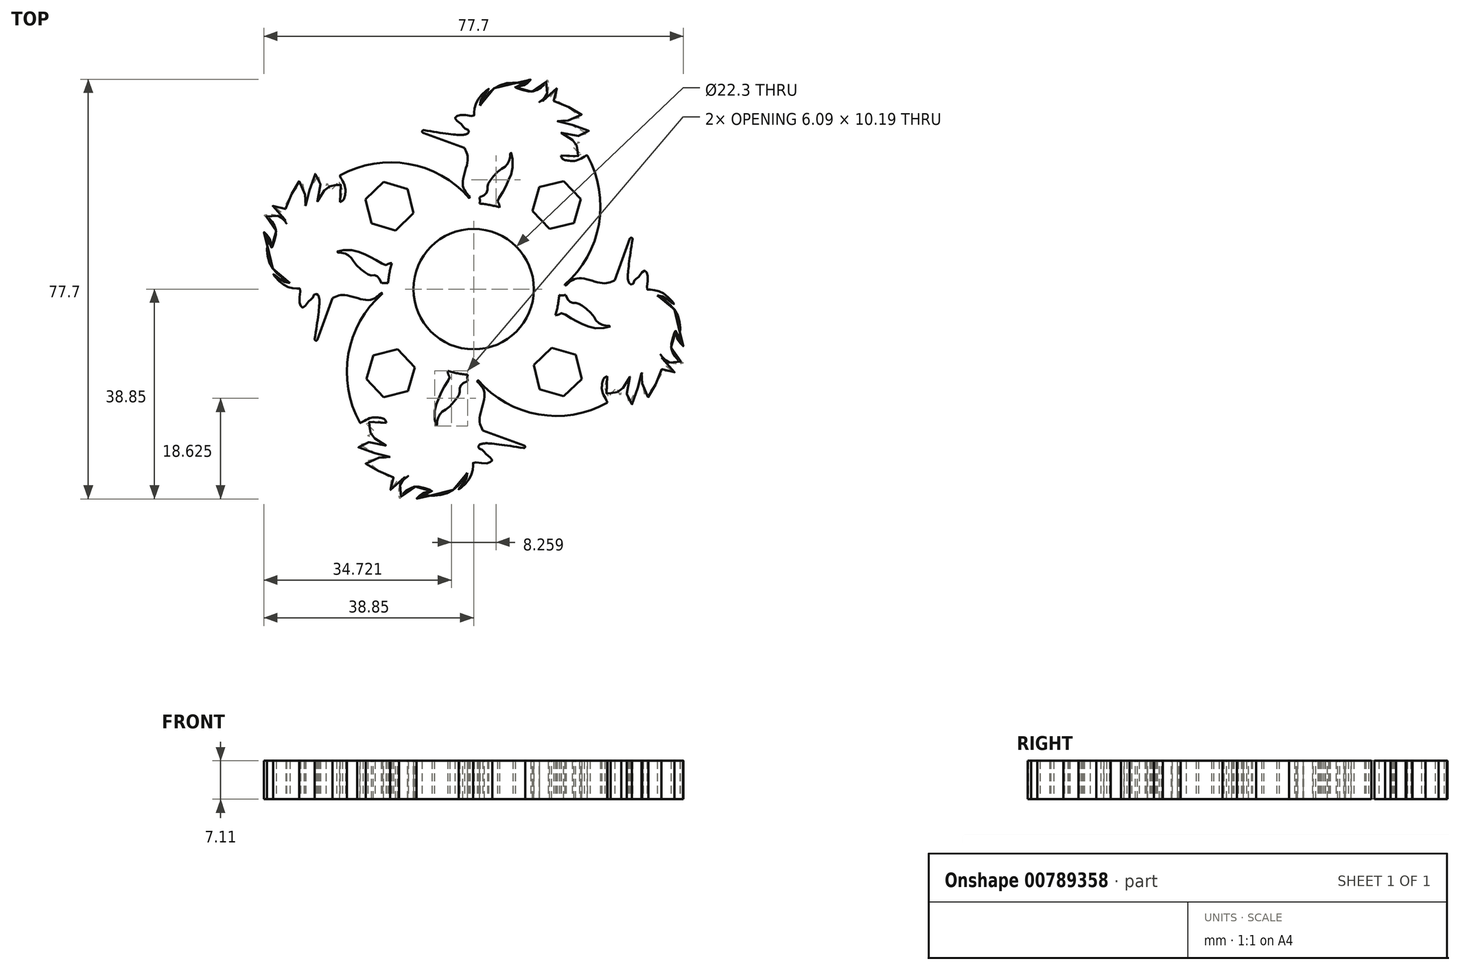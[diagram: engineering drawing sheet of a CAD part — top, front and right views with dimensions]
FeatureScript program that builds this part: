
annotation { "Feature Type Name" : "Feature", "Feature Type Description" : "" }
export const myFeature = defineFeature(function(context is Context, id is Id, definition is map)
    precondition{}
    {
        {
            var Q0;
            Q0=qCreatedBy(makeId("Top.planeOp"),FACE);
            var sketch = newSketch(context, id + "F0", { "sketchPlane" : qUnion([Q0])});
            skCircle(sketch, "E0", {"center": v(0, 0) * mm, "radius": 11.15 * mm});
            skLineSegment(sketch, "E1", {"start": v(-24.57, 4.35) * mm, "end": v(-20.17, 10.05) * mm});
            skFitSpline(sketch, "E2", {"points": [v(-20.17, 10.05) * mm, v(-18.6, 9.94) * mm, v(-15.83, 8.42) * mm, v(-13.83, 9.06) * mm], "startDerivative": vector(5.21, 0.73) * mm, "endDerivative": vector(5.8, 3.1) * mm});
            skFitSpline(sketch, "E3", {"points": [v(-21.73, 10.94) * mm, v(-21.9, 11.16) * mm, v(-22.2, 11.13) * mm, v(-22.5, 10.76) * mm, v(-22.9, 10.66) * mm, v(-23.94, 10.03) * mm, v(-24.16, 10.26) * mm, v(-24.15, 11) * mm, v(-23.6, 12.33) * mm, v(-23.83, 12.46) * mm, v(-24.69, 12.84) * mm, v(-25.7, 13.9) * mm, v(-26.21, 15.08) * mm, v(-25.72, 14.44) * mm, v(-24.6, 13.44) * mm], "startDerivative": vector(-3.17, 6.23) * mm, "endDerivative": vector(14.4, -3.3) * mm});
            skFitSpline(sketch, "E4", {"points": [v(-24.6, 13.44) * mm, v(-25.33, 14.36) * mm, v(-26.15, 16.1) * mm, v(-26.07, 18.07) * mm, v(-25.72, 19.07) * mm, v(-25.69, 19.78) * mm, v(-25.75, 20.4) * mm, v(-25.54, 20.07) * mm, v(-25.3, 19.05) * mm, v(-25.4, 18.27) * mm, v(-25.03, 18.7) * mm, v(-24.28, 19.98) * mm, v(-24.28, 20.88) * mm, v(-24.65, 21.87) * mm, v(-25.05, 22.32) * mm, v(-24.8, 22.35) * mm, v(-23.66, 21.93) * mm, v(-22.9, 21) * mm, v(-22.74, 20.53) * mm, v(-22.83, 21.43) * mm, v(-23.24, 22.55) * mm, v(-23.71, 23.15) * mm, v(-23.4, 23.08) * mm, v(-22.66, 22.69) * mm, v(-22.32, 22.3) * mm, v(-22.2, 22.57) * mm, v(-21.49, 23.56) * mm, v(-20.6, 23.98) * mm, v(-19.98, 24.29) * mm, v(-19.7, 25.05) * mm, v(-19.48, 24.85) * mm, v(-19.34, 24.17) * mm, v(-19.56, 23.08) * mm, v(-19.9, 22.45) * mm, v(-19.92, 21.83) * mm, v(-19.77, 22.07) * mm, v(-19.54, 22.84) * mm, v(-19.1, 23.35) * mm, v(-18.25, 23.98) * mm, v(-17.72, 24.53) * mm, v(-17.42, 25.42) * mm, v(-17.2, 25.15) * mm, v(-17.17, 24.49) * mm, v(-17.5, 23.32) * mm, v(-18.08, 22.55) * mm, v(-18.3, 21.99) * mm, v(-18.14, 22.2) * mm, v(-17.7, 22.6) * mm, v(-17.04, 23.03) * mm, v(-16.8, 23.18) * mm, v(-16.56, 23.76) * mm, v(-16.33, 23.57) * mm, v(-16.27, 22.94) * mm, v(-16.3, 22.75) * mm, v(-15.83, 22.91) * mm, v(-15.39, 23.3) * mm, v(-15.14, 23.95) * mm, v(-15.03, 23.57) * mm, v(-14.9, 22.84) * mm, v(-15.1, 21.82) * mm, v(-15.66, 21.08) * mm], "startDerivative": vector(-33.95, 39.33) * mm, "endDerivative": vector(-32.89, -35.92) * mm});
            skFitSpline(sketch, "E5", {"points": [v(-15.66, 21.08) * mm, v(-15.17, 21.19) * mm, v(-14.76, 21.8) * mm, v(-14.5, 22.9) * mm, v(-14.68, 24.18) * mm, v(-14.25, 23.59) * mm, v(-14, 22) * mm, v(-14.5, 20.36) * mm, v(-14.57, 19.83) * mm, v(-13.94, 18.55) * mm, v(-13.41, 17.15) * mm, v(-12.84, 15.14) * mm, v(-12.49, 12.77) * mm, v(-12.64, 11.92) * mm, v(-13.48, 12.77) * mm, v(-14.73, 14) * mm, v(-16.34, 15.07) * mm, v(-17.93, 15.31) * mm, v(-17.66, 15.14) * mm, v(-17.17, 14.94) * mm, v(-16.75, 14.58) * mm, v(-16.42, 14.04) * mm, v(-16.26, 13.35) * mm, v(-15.56, 12.1) * mm, v(-15.13, 11.54) * mm, v(-14.8, 11.28) * mm, v(-14.4, 11.16) * mm, v(-14.07, 10.94) * mm, v(-13.86, 10.42) * mm, v(-13.83, 9.06) * mm], "startDerivative": vector(21.3, 0.89) * mm, "endDerivative": vector(-1, -37.46) * mm});
            skFitSpline(sketch, "E6", {"points": [v(-21.73, 10.94) * mm, v(-21.72, 10.6) * mm, v(-21.92, 9.84) * mm, v(-24.57, 4.35) * mm], "startDerivative": vector(0.16, -2.17) * mm, "endDerivative": vector(-5.4, -10.67) * mm});
            skLineSegment(sketch, "E7.0", {"start": v(-15.45, 21.3) * mm, "end": v(-15.17, 21.19) * mm, "construction": true});
            skLineSegment(sketch, "E8.0", {"start": v(-22.2, 11.13) * mm, "end": v(-21.73, 10.94) * mm, "construction": true});
            skArc(sketch, "E9", {"start": v(0, 15.88) * mm, "mid": v(-5.79, 22.77) * mm, "end": v(-14.68, 24.18) * mm});
            skCircle(sketch, "E10", {"center": v(0, 0) * mm, "radius": 15.88 * mm});
            skArc(sketch, "E11", {"start": v(-11.09, 11.36) * mm, "mid": v(-11.77, 11.9) * mm, "end": v(-12.64, 11.92) * mm});
            skArc(sketch, "E12", {"start": v(-12.72, 9.5) * mm, "mid": v(-13.24, 9.8) * mm, "end": v(-13.82, 9.94) * mm});
            skArc(sketch, "E13", {"start": v(-13.54, 8.29) * mm, "mid": v(-13.89, 8.57) * mm, "end": v(-14.24, 8.84) * mm});
            skLineSegment(sketch, "E14", {"start": v(0, 15.88) * mm, "end": v(0, 11.15) * mm});
            skLineSegment(sketch, "E15", {"start": v(-15.88, 0) * mm, "end": v(-11.15, 0) * mm});
            skArc(sketch, "E16", {"start": v(0, 11.15) * mm, "mid": v(-7.88, 7.88) * mm, "end": v(-11.15, 0) * mm});
            skArc(sketch, "E17", {"start": v(0, 15.88) * mm, "mid": v(-11.23, 11.23) * mm, "end": v(-15.88, 0) * mm});
            skSolve(sketch);
        }
        {
            var Q0;
            {var subQ0=sQuery(id+"F0.wireOp",EDGE,"E9");var subQ1=sQuery(id+"F0.wireOp",EDGE,"E5");var subQ2=makeQuery(id+"F0.imprint","INTERSECT",VERTEX,{"disambiguationData":[OD(0.0)],"derivedFrom":[subQ1,subQ0]});Q0=makeQuery(id+"F0.imprint","IMPRINT",FACE,{"disambiguationData":[TD([[makeQuery(id+"F0.imprint","IMPRINT",EDGE,{"disambiguationData":[TD([[subQ2,-1.0]])],"derivedFrom":subQ1}),-1.0]])]});}
            var Q1;
            {var subQ0=sQuery(id+"F0.wireOp",EDGE,"E12");Q1=makeQuery(id+"F0.imprint","IMPRINT",FACE,{"disambiguationData":[TD([[makeQuery(id+"F0.imprint","IMPRINT",EDGE,{"derivedFrom":subQ0}),1.0]])]});}
            var Q2;
            {var subQ0=sQuery(id+"F0.wireOp",EDGE,"E9");var subQ1=sQuery(id+"F0.wireOp",EDGE,"E5");var subQ2=makeQuery(id+"F0.imprint","INTERSECT",VERTEX,{"disambiguationData":[OD(1.0)],"derivedFrom":[subQ1,subQ0]});Q2=makeQuery(id+"F0.imprint","IMPRINT",FACE,{"disambiguationData":[TD([[makeQuery(id+"F0.imprint","IMPRINT",EDGE,{"disambiguationData":[TD([[subQ2,-1.0]])],"derivedFrom":subQ1}),1.0]])]});}
            var Q3;
            {var subQ11=sQuery(id+"F0.wireOp",EDGE,"E1");Q3=makeQuery(id+"F0.imprint","IMPRINT",FACE,{"disambiguationData":[TD([[makeQuery(id+"F0.imprint","IMPRINT",EDGE,{"derivedFrom":subQ11}),1.0]])]});}
            extrude(context, id + "F1", {"entities" : qUnion([Q0, Q1, Q2, Q3]), "depth" : 10.16 * mm, "offsetDistance" : 25.4 * mm});
        }
        {
            var Q0;
            Q0=qCreatedBy(makeId("Front.planeOp"),FACE);
            var sketch = newSketch(context, id + "F2", { "sketchPlane" : qUnion([Q0])});
            skLineSegment(sketch, "E18", {"start": v(0, 34.97) * mm, "end": v(0, -32.82) * mm, "construction": true});
            skSolve(sketch);
        }
        {
            var Q0;
            Q0=makeQuery(id+"F1.opExtrude","SWEPT_BODY",BODY,{"disambiguationData":[OSD([sQuery(id+"F0.wireOp",EDGE,"E1"),sQuery(id+"F0.wireOp",EDGE,"E2"),sQuery(id+"F0.wireOp",EDGE,"E3"),sQuery(id+"F0.wireOp",EDGE,"E4"),sQuery(id+"F0.wireOp",EDGE,"E5"),sQuery(id+"F0.wireOp",EDGE,"E6"),sQuery(id+"F0.wireOp",EDGE,"E9"),sQuery(id+"F0.wireOp",EDGE,"E10"),sQuery(id+"F0.wireOp",EDGE,"E11"),sQuery(id+"F0.wireOp",EDGE,"E12"),sQuery(id+"F0.wireOp",EDGE,"E13")])]});
            var Q1;
            Q1=makeQuery(id+"F1.opExtrude","CAP_VERTEX",VERTEX,{"disambiguationData":[OSD([sQuery(id+"F0.wireOp",EDGE,"E9"),sQuery(id+"F0.wireOp",EDGE,"E10"),sQuery(id+"F0.wireOp",EDGE,"E14")])],"isStart":true});
            transform(context, id + "F3", {"entities" : qUnion([Q0]), "transformType" : TransformType.SCALE_UNIFORMLY, "scale" : 1.5, "scalePoint" : qUnion([Q1]), "makeCopy" : false});
        }
        {
            var Q0;
            Q0=makeQuery(id+"F1.opExtrude","SWEPT_BODY",BODY,{"disambiguationData":[OSD([sQuery(id+"F0.wireOp",EDGE,"E1"),sQuery(id+"F0.wireOp",EDGE,"E2"),sQuery(id+"F0.wireOp",EDGE,"E3"),sQuery(id+"F0.wireOp",EDGE,"E4"),sQuery(id+"F0.wireOp",EDGE,"E5"),sQuery(id+"F0.wireOp",EDGE,"E6"),sQuery(id+"F0.wireOp",EDGE,"E9"),sQuery(id+"F0.wireOp",EDGE,"E10"),sQuery(id+"F0.wireOp",EDGE,"E11"),sQuery(id+"F0.wireOp",EDGE,"E12"),sQuery(id+"F0.wireOp",EDGE,"E13")])]});
            var Q1;
            Q1=makeQuery(id+"F1.opExtrude","SWEPT_EDGE",EDGE,{"disambiguationData":[OSD([sQuery(id+"F0.wireOp",EDGE,"E9"),sQuery(id+"F0.wireOp",EDGE,"E10"),sQuery(id+"F0.wireOp",EDGE,"E14")])]});
            transform(context, id + "F4", {"entities" : qUnion([Q0]), "transformType" : TransformType.ROTATION, "transformAxis" : qUnion([Q1]), "angle" : 17.74 * degree, "oppositeDirection" : true, "makeCopy" : false});
        }
        {
            var Q0;
            {var subQ0=sQuery(id+"F0.wireOp",EDGE,"E14");Q0=makeQuery(id+"F0.imprint","IMPRINT",FACE,{"disambiguationData":[TD([[makeQuery(id+"F0.imprint","IMPRINT",EDGE,{"derivedFrom":subQ0}),1.0]])]});}
            var Q1;
            {var subQ4=sQuery(id+"F0.wireOp",EDGE,"E14");Q1=makeQuery(id+"F0.imprint","IMPRINT",FACE,{"disambiguationData":[TD([[makeQuery(id+"F0.imprint","IMPRINT",EDGE,{"derivedFrom":subQ4}),-1.0]])]});}
            extrude(context, id + "F5", {"entities" : qUnion([Q0, Q1]), "operationType" : NewBodyOperationType.ADD, "depth" : 7.11 * mm, "offsetDistance" : 25.4 * mm});
        }
        {
            var Q0;
            Q0=makeQuery(id+"F1.opExtrude","SWEPT_BODY",BODY,{"disambiguationData":[OSD([sQuery(id+"F0.wireOp",EDGE,"E1"),sQuery(id+"F0.wireOp",EDGE,"E2"),sQuery(id+"F0.wireOp",EDGE,"E3"),sQuery(id+"F0.wireOp",EDGE,"E4"),sQuery(id+"F0.wireOp",EDGE,"E5"),sQuery(id+"F0.wireOp",EDGE,"E6"),sQuery(id+"F0.wireOp",EDGE,"E9"),sQuery(id+"F0.wireOp",EDGE,"E10"),sQuery(id+"F0.wireOp",EDGE,"E11"),sQuery(id+"F0.wireOp",EDGE,"E12"),sQuery(id+"F0.wireOp",EDGE,"E13")])]});
            var Q1;
            Q1=sQuery(id+"F2.wireOp",EDGE,"E18");
            circularPattern(context, id + "F6", {"operationType" : NewBodyOperationType.ADD, "entities" : qUnion([Q0]), "axis" : qUnion([Q1]), "angle" : 360 * degree, "instanceCount" : 4, "equalSpace" : true});
        }
        {
            var Q0;
            {var subQ0=makeQuery(id+"F1.opExtrude","CAP_FACE",FACE,{"disambiguationData":[OSD([sQuery(id+"F0.wireOp",EDGE,"E1"),sQuery(id+"F0.wireOp",EDGE,"E2"),sQuery(id+"F0.wireOp",EDGE,"E3"),sQuery(id+"F0.wireOp",EDGE,"E4"),sQuery(id+"F0.wireOp",EDGE,"E5"),sQuery(id+"F0.wireOp",EDGE,"E6"),sQuery(id+"F0.wireOp",EDGE,"E9"),sQuery(id+"F0.wireOp",EDGE,"E10"),sQuery(id+"F0.wireOp",EDGE,"E11"),sQuery(id+"F0.wireOp",EDGE,"E12"),sQuery(id+"F0.wireOp",EDGE,"E13")])],"isStart":false});Q0=makeQuery(id+"F6.boolean.opBoolean","MERGE",FACE,{"derivedFrom":[subQ0,makeQuery(id+"F6.opPattern","COPY",FACE,{"derivedFrom":subQ0,"instanceName":"1"}),makeQuery(id+"F6.opPattern","COPY",FACE,{"derivedFrom":subQ0,"instanceName":"2"}),makeQuery(id+"F6.opPattern","COPY",FACE,{"derivedFrom":subQ0,"instanceName":"3"})]});}
            var sketch = newSketch(context, id + "F7", { "sketchPlane" : qUnion([Q0])});
            skCircle(sketch, "E19.cCircle", {"center": v(-15.57, 15.35) * mm, "radius": 4.62 * mm, "construction": true});
            skLineSegment(sketch, "E19.0", {"start": v(-11.13, 14.06) * mm, "end": v(-14.47, 10.87) * mm});
            skLineSegment(sketch, "E19.1", {"start": v(-14.47, 10.87) * mm, "end": v(-18.9, 12.15) * mm});
            skLineSegment(sketch, "E19.2", {"start": v(-18.9, 12.15) * mm, "end": v(-20, 16.64) * mm});
            skLineSegment(sketch, "E19.3", {"start": v(-20, 16.64) * mm, "end": v(-16.67, 19.84) * mm});
            skLineSegment(sketch, "E19.4", {"start": v(-16.67, 19.84) * mm, "end": v(-12.24, 18.55) * mm});
            skLineSegment(sketch, "E19.5", {"start": v(-12.24, 18.55) * mm, "end": v(-11.13, 14.06) * mm});
            skCircle(sketch, "E20.1.0", {"center": v(-15.35, -15.57) * mm, "radius": 4.62 * mm, "construction": true});
            skLineSegment(sketch, "E20.1.1", {"start": v(-12.15, -18.9) * mm, "end": v(-16.64, -20) * mm});
            skLineSegment(sketch, "E20.1.2", {"start": v(-14.06, -11.13) * mm, "end": v(-10.87, -14.47) * mm});
            skLineSegment(sketch, "E20.1.3", {"start": v(-18.55, -12.24) * mm, "end": v(-14.06, -11.13) * mm});
            skLineSegment(sketch, "E20.1.4", {"start": v(-19.84, -16.67) * mm, "end": v(-18.55, -12.24) * mm});
            skLineSegment(sketch, "E20.1.5", {"start": v(-16.64, -20) * mm, "end": v(-19.84, -16.67) * mm});
            skLineSegment(sketch, "E20.1.6", {"start": v(-10.87, -14.47) * mm, "end": v(-12.15, -18.9) * mm});
            skCircle(sketch, "E20.2.0", {"center": v(15.57, -15.35) * mm, "radius": 4.62 * mm, "construction": true});
            skLineSegment(sketch, "E20.2.1", {"start": v(18.9, -12.15) * mm, "end": v(20, -16.64) * mm});
            skLineSegment(sketch, "E20.2.2", {"start": v(11.13, -14.06) * mm, "end": v(14.47, -10.87) * mm});
            skLineSegment(sketch, "E20.2.3", {"start": v(12.24, -18.55) * mm, "end": v(11.13, -14.06) * mm});
            skLineSegment(sketch, "E20.2.4", {"start": v(16.67, -19.84) * mm, "end": v(12.24, -18.55) * mm});
            skLineSegment(sketch, "E20.2.5", {"start": v(20, -16.64) * mm, "end": v(16.67, -19.84) * mm});
            skLineSegment(sketch, "E20.2.6", {"start": v(14.47, -10.87) * mm, "end": v(18.9, -12.15) * mm});
            skCircle(sketch, "E20.3.0", {"center": v(15.35, 15.57) * mm, "radius": 4.62 * mm, "construction": true});
            skLineSegment(sketch, "E20.3.1", {"start": v(12.15, 18.9) * mm, "end": v(16.64, 20) * mm});
            skLineSegment(sketch, "E20.3.2", {"start": v(14.06, 11.13) * mm, "end": v(10.87, 14.47) * mm});
            skLineSegment(sketch, "E20.3.3", {"start": v(18.55, 12.24) * mm, "end": v(14.06, 11.13) * mm});
            skLineSegment(sketch, "E20.3.4", {"start": v(19.84, 16.67) * mm, "end": v(18.55, 12.24) * mm});
            skLineSegment(sketch, "E20.3.5", {"start": v(16.64, 20) * mm, "end": v(19.84, 16.67) * mm});
            skLineSegment(sketch, "E20.3.6", {"start": v(10.87, 14.47) * mm, "end": v(12.15, 18.9) * mm});
            skPoint(sketch, "E20.center", {"position": v(0, 0) * mm});
            skSolve(sketch);
        }
        {
            var Q0;
            Q0 = qSketchRegion(id + "F7", true);
            extrude(context, id + "F8", {"entities" : qUnion([Q0]), "operationType" : NewBodyOperationType.REMOVE, "endBound" : BoundingType.THROUGH_ALL, "oppositeDirection" : true, "depth" : 25.4 * mm, "offsetDistance" : 25.4 * mm});
        }
        {
            var Q0;
            Q0=makeQuery(id+"F5.opExtrude","CAP_FACE",FACE,{"disambiguationData":[OSD([sQuery(id+"F0.wireOp",EDGE,"E0"),sQuery(id+"F0.wireOp",EDGE,"E10")])],"isStart":false});
            var sketch = newSketch(context, id + "F9", { "sketchPlane" : qUnion([Q0])});
            skLineSegment(sketch, "E21", {"start": v(0, 39.02) * mm, "end": v(0, -42.42) * mm, "construction": true});
            skSolve(sketch);
        }
        {
            var Q0;
            Q0=qCreatedBy(makeId("Right.planeOp"),FACE);
            var sketch = newSketch(context, id + "F10", { "sketchPlane" : qUnion([Q0])});
            skLineSegment(sketch, "E22.bottom", {"start": v(-42.42, 7.11) * mm, "end": v(49.44, 7.11) * mm});
            skLineSegment(sketch, "E22.top", {"start": v(-42.42, 20.32) * mm, "end": v(49.44, 20.32) * mm});
            skLineSegment(sketch, "E22.left", {"start": v(-42.42, 7.11) * mm, "end": v(-42.42, 20.32) * mm});
            skLineSegment(sketch, "E22.right", {"start": v(49.44, 7.11) * mm, "end": v(49.44, 20.32) * mm});
            skSolve(sketch);
        }
        {
            var Q0;
            Q0 = qSketchRegion(id + "F10", true);
            extrude(context, id + "F11", {"entities" : qUnion([Q0]), "operationType" : NewBodyOperationType.REMOVE, "endBound" : BoundingType.THROUGH_ALL, "oppositeDirection" : true, "depth" : 25.4 * mm, "offsetDistance" : 25.4 * mm, "hasSecondDirection" : true, "secondDirectionBound" : SecondDirectionBoundingType.THROUGH_ALL, "secondDirectionOppositeDirection" : false, "secondDirectionDepth" : 25.4 * mm});
        }
        {
            var Q0;
            Q0=makeQuery(id+"F1.opExtrude","SWEPT_EDGE",EDGE,{"disambiguationData":[OSD([sQuery(id+"F0.wireOp",EDGE,"E1"),sQuery(id+"F0.wireOp",EDGE,"E6")])]});
            var Q1;
            Q1=makeQuery(id+"F6.opPattern","COPY",EDGE,{"derivedFrom":makeQuery(id+"F1.opExtrude","SWEPT_EDGE",EDGE,{"disambiguationData":[OSD([sQuery(id+"F0.wireOp",EDGE,"E1"),sQuery(id+"F0.wireOp",EDGE,"E6")])]}),"instanceName":"3"});
            var Q2;
            Q2=makeQuery(id+"F6.opPattern","COPY",EDGE,{"derivedFrom":makeQuery(id+"F1.opExtrude","SWEPT_EDGE",EDGE,{"disambiguationData":[OSD([sQuery(id+"F0.wireOp",EDGE,"E1"),sQuery(id+"F0.wireOp",EDGE,"E6")])]}),"instanceName":"2"});
            var Q3;
            Q3=makeQuery(id+"F6.opPattern","COPY",EDGE,{"derivedFrom":makeQuery(id+"F1.opExtrude","SWEPT_EDGE",EDGE,{"disambiguationData":[OSD([sQuery(id+"F0.wireOp",EDGE,"E1"),sQuery(id+"F0.wireOp",EDGE,"E6")])]}),"instanceName":"1"});
            fillet(context, id + "F12", {"entities" : qUnion([Q0, Q1, Q2, Q3]), "radius" : .25 * mm, "tangentPropagation" : true, "allowEdgeOverflow" : false});
        }
    });
